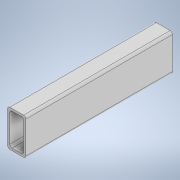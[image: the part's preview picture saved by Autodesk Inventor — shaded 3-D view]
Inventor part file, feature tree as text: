
AUTODESK INVENTOR PART (.ipt)
format: ipt  version: 2020 (Build 240168000, 168)  size: 121,856 bytes
history: native  units: in
note: dims shown in document units (in); Inventor stores cm internally (conversion verified against a paired STEP export)
features: extrude x1, sketch x1
ambient origin geometry x8: Origin, YZ Plane, XZ Plane, XY Plane, X Axis, Y Axis, Z Axis, Center Point
bodies: Solid1 (feature_tree)
feature tree (2):
  extrude  "Extrusion1"  Depth=1.0in
  sketch  "Sketch1"  dims[d0=2.0in d1=1.0in d2=0.125in d3=0.125in d4=0.125in d5=0.125in d6=0.125in d7=0.125in d8=0.125in d9=0.125in d10=0.125in d11=8.0in d12=0.0in]
